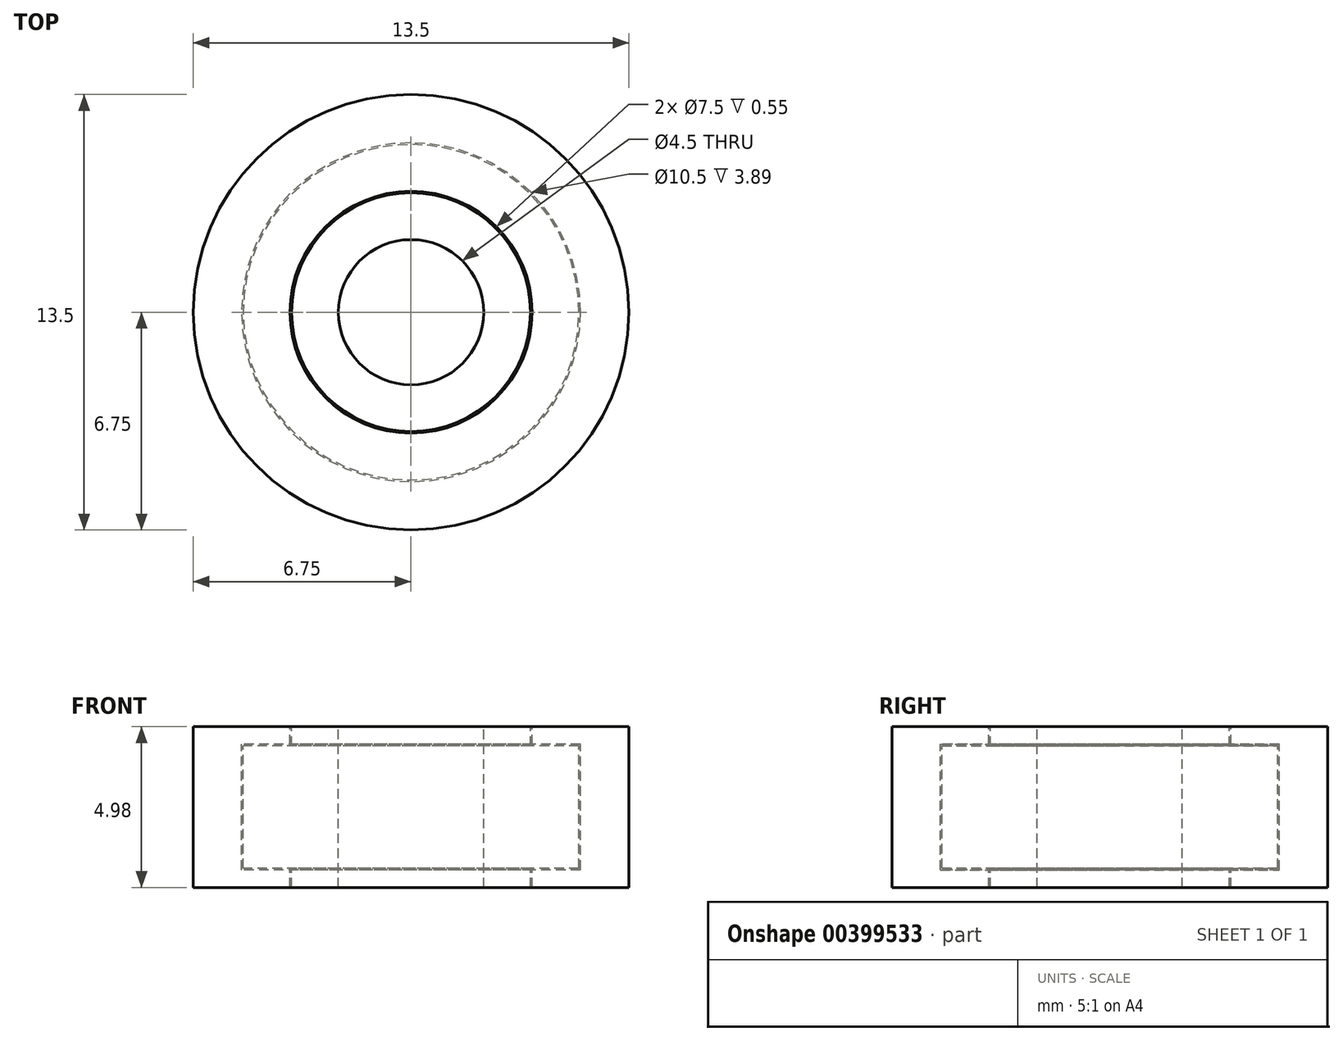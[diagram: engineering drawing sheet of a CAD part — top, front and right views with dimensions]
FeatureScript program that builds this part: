
annotation { "Feature Type Name" : "Feature", "Feature Type Description" : "" }
export const myFeature = defineFeature(function(context is Context, id is Id, definition is map)
    precondition{}
    {
        {
            var Q0;
            Q0=qCreatedBy(makeId("Front.planeOp"),FACE);
            var sketch = newSketch(context, id + "F0", { "sketchPlane" : qUnion([Q0])});
            skLineSegment(sketch, "E0.bottom", {"start": v(2.25, -2.5) * mm, "end": v(0, -2.5) * mm});
            skLineSegment(sketch, "E0.top", {"start": v(2.25, 2.5) * mm, "end": v(0, 2.5) * mm});
            skLineSegment(sketch, "E0.left", {"start": v(2.25, -2.5) * mm, "end": v(2.25, 2.5) * mm});
            skPoint(sketch, "E0.middle", {"position": v(0, 0) * mm});
            skLineSegment(sketch, "E1.bottom", {"start": v(6.75, -2.5) * mm, "end": v(3.75, -2.5) * mm});
            skLineSegment(sketch, "E1.top", {"start": v(6.75, 2.5) * mm, "end": v(3.75, 2.5) * mm});
            skLineSegment(sketch, "E1.left", {"start": v(6.75, -2.5) * mm, "end": v(6.75, 2.5) * mm});
            skLineSegment(sketch, "E2", {"start": v(0, 2.5) * mm, "end": v(0, -2.5) * mm, "construction": true});
            skPoint(sketch, "E0.right.start.orphan", {"position": v(-2.25, -2.5) * mm});
            skPoint(sketch, "E1.right.end.orphan", {"position": v(-6.75, 2.5) * mm});
            skPoint(sketch, "E1.right.start.orphan", {"position": v(-6.75, -2.5) * mm});
            skPoint(sketch, "E3.orphan", {"position": v(-2.25, 2.5) * mm});
            skLineSegment(sketch, "E4.bottom", {"start": v(3.75, 1.9) * mm, "end": v(5.2, 1.9) * mm});
            skLineSegment(sketch, "E4.top", {"start": v(3.75, -1.9) * mm, "end": v(5.2, -1.9) * mm});
            skLineSegment(sketch, "E4.left", {"start": v(2.25, 1.9) * mm, "end": v(2.25, -1.9) * mm});
            skLineSegment(sketch, "E4.right", {"start": v(5.2, 1.9) * mm, "end": v(5.2, -1.9) * mm});
            skLineSegment(sketch, "E5.bottom", {"start": v(3.75, 1.94) * mm, "end": v(5.25, 1.94) * mm});
            skLineSegment(sketch, "E5.top", {"start": v(3.75, -1.94) * mm, "end": v(5.25, -1.94) * mm});
            skLineSegment(sketch, "E5.left", {"start": v(2.25, 1.94) * mm, "end": v(2.25, -1.94) * mm});
            skLineSegment(sketch, "E5.right", {"start": v(5.25, 1.94) * mm, "end": v(5.25, -1.94) * mm});
            skLineSegment(sketch, "E6", {"start": v(3.75, 2.5) * mm, "end": v(3.75, 1.94) * mm});
            skPoint(sketch, "E6.startSnap0", {"position": v(3.75, 1.94) * mm});
            skLineSegment(sketch, "E7.trimOffspring", {"start": v(3.75, -1.94) * mm, "end": v(3.75, -2.5) * mm});
            skLineSegment(sketch, "E8", {"start": v(3.7, 2.5) * mm, "end": v(3.7, 1.9) * mm});
            skLineSegment(sketch, "E9", {"start": v(3.75, 1.9) * mm, "end": v(3.7, 1.9) * mm});
            skLineSegment(sketch, "E10", {"start": v(3.7, -1.9) * mm, "end": v(3.75, -1.9) * mm});
            skLineSegment(sketch, "E11.trimOffspring", {"start": v(3.7, -1.9) * mm, "end": v(3.7, -2.5) * mm});
            skLineSegment(sketch, "E12.trimOffspring", {"start": v(3.7, 2.5) * mm, "end": v(0, 2.5) * mm});
            skLineSegment(sketch, "E13.trimOffspring", {"start": v(3.7, -2.5) * mm, "end": v(0, -2.5) * mm});
            skSolve(sketch);
        }
        {
            var Q0;
            Q0=qSketchRegion(id+"F0",true);
            var Q1;
            Q1=sQuery(id+"F0.wireOp",EDGE,"E2");
            revolve(context, id + "F1", {"entities" : qUnion([Q0]), "axis" : qUnion([Q1]), "revolveType" : RevolveType.FULL});
        }
    });
